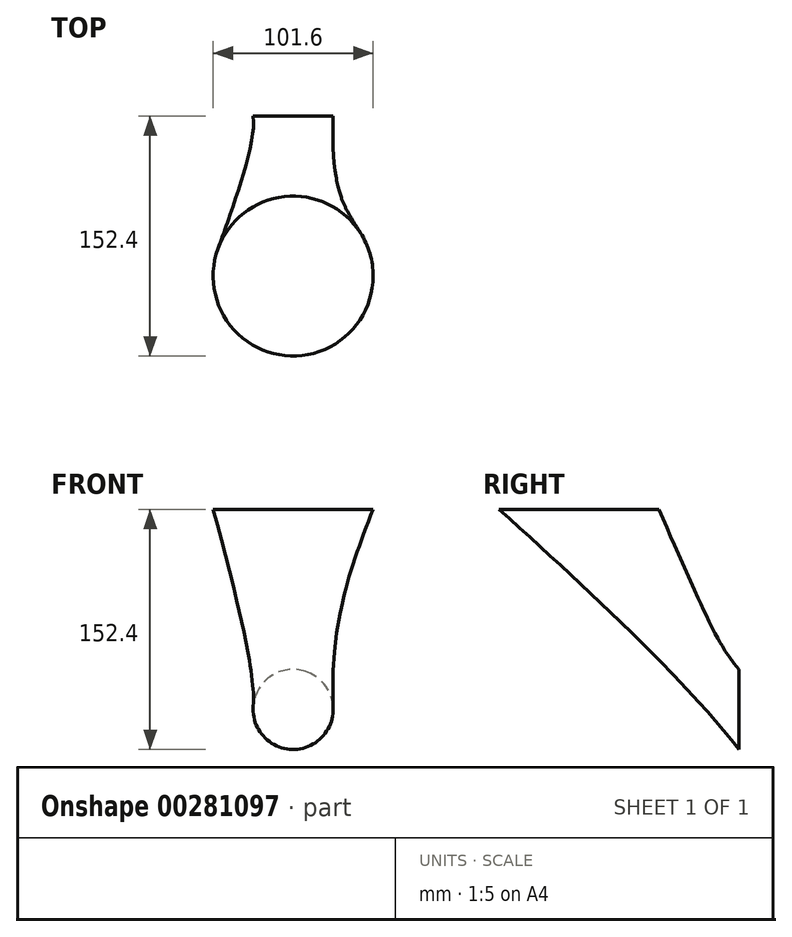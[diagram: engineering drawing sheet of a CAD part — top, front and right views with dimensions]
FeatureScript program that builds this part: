
annotation { "Feature Type Name" : "Feature", "Feature Type Description" : "" }
export const myFeature = defineFeature(function(context is Context, id is Id, definition is map)
    precondition{}
    {
        {
            var Q0;
            Q0=qCreatedBy(makeId("Front.planeOp"),FACE);
            var sketch = newSketch(context, id + "F0", { "sketchPlane" : qUnion([Q0])});
            skCircle(sketch, "E0", {"center": v(0, 0) * mm, "radius": 25.4 * mm});
            skSolve(sketch);
        }
        {
            var Q0;
            Q0=qCreatedBy(makeId("Top.planeOp"),FACE);
            cPlane(context, id + "F1", {"entities" : qUnion([Q0]), "cplaneType" : CPlaneType.OFFSET, "offset" : 127 * mm, "width" : 152.4 * mm, "height" : 152.4 * mm});
        }
        {
            var Q0;
            Q0=qCreatedBy(id+"F1.planeOp",FACE);
            var sketch = newSketch(context, id + "F2", { "sketchPlane" : qUnion([Q0])});
            skCircle(sketch, "E1", {"center": v(0, -101.6) * mm, "radius": 50.8 * mm});
            skSolve(sketch);
        }
        {
            var Q0;
            Q0=makeQuery(id+"F2.imprint","IMPRINT",FACE,{"disambiguationData":[TD([[makeQuery(id+"F2.imprint","IMPRINT",EDGE,{"derivedFrom":sQuery(id+"F2.wireOp",EDGE,"E1")}),1.0]])]});
            var Q1;
            Q1=makeQuery(id+"F0.imprint","IMPRINT",FACE,{"disambiguationData":[TD([[makeQuery(id+"F0.imprint","IMPRINT",EDGE,{"derivedFrom":sQuery(id+"F0.wireOp",EDGE,"E0")}),1.0]])]});
            loft(context, id + "F3", {"sheetProfilesArray" : [{ "sheetProfileEntities" : qUnion([Q0]) }, { "sheetProfileEntities" : qUnion([Q1]) }]});
        }
    });
